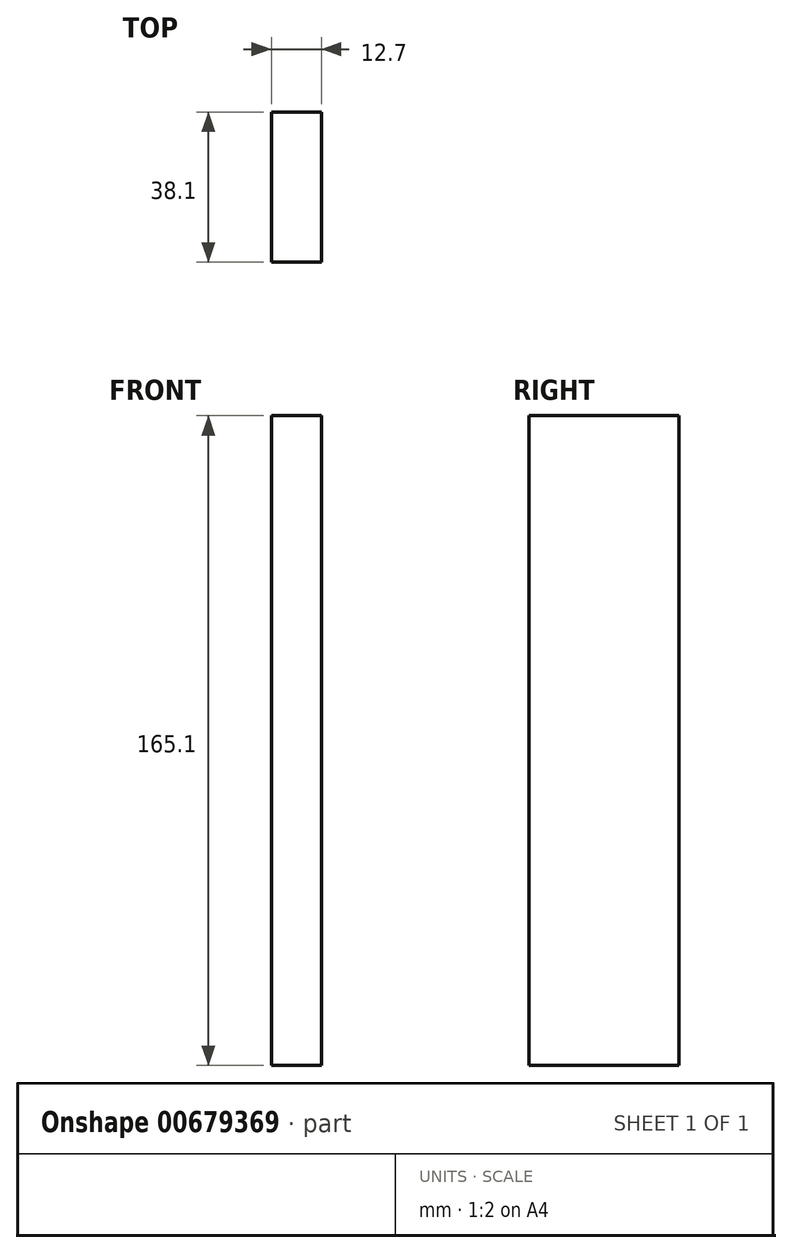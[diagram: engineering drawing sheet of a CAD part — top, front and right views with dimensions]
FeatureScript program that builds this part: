
annotation { "Feature Type Name" : "Feature", "Feature Type Description" : "" }
export const myFeature = defineFeature(function(context is Context, id is Id, definition is map)
    precondition{}
    {
        {
            var Q0;
            Q0=qCreatedBy(makeId("Right.planeOp"),FACE);
            var sketch = newSketch(context, id + "F0", { "sketchPlane" : qUnion([Q0])});
            skLineSegment(sketch, "E0.bottom", {"start": v(19.05, 82.55) * mm, "end": v(-19.05, 82.55) * mm});
            skLineSegment(sketch, "E0.top", {"start": v(19.05, -82.55) * mm, "end": v(-19.05, -82.55) * mm});
            skLineSegment(sketch, "E0.left", {"start": v(19.05, 82.55) * mm, "end": v(19.05, -82.55) * mm});
            skLineSegment(sketch, "E0.right", {"start": v(-19.05, 82.55) * mm, "end": v(-19.05, -82.55) * mm});
            skPoint(sketch, "E0.middle", {"position": v(0, 0) * mm});
            skSolve(sketch);
        }
        {
            var Q0;
            Q0 = qSketchRegion(id + "F0", true);
            extrude(context, id + "F1", {"entities" : qUnion([Q0]), "depth" : 12.7 * mm, "offsetDistance" : 25.4 * mm});
        }
    });
